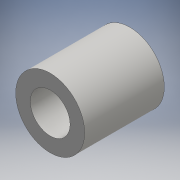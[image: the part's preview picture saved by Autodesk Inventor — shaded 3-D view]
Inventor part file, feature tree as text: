
AUTODESK INVENTOR PART (.ipt)
format: ipt  version: 2016 (Build 200138000, 138)  size: 97,280 bytes
history: native  units: mm
features: extrude x2, sketch x2, other x1
ambient origin geometry x8: Origin, YZ Plane, XZ Plane, XY Plane, X Axis, Y Axis, Z Axis, Center Point
bodies: Body1 (feature_tree)
feature tree (5):
  other  "ソリッド1"
  extrude  "押し出し1"  Depth=52.0mm
  extrude  "押し出し2"  Depth=60.0mm TaperAngle=0.0deg
  sketch  "スケッチ1"
  sketch  "スケッチ2"
